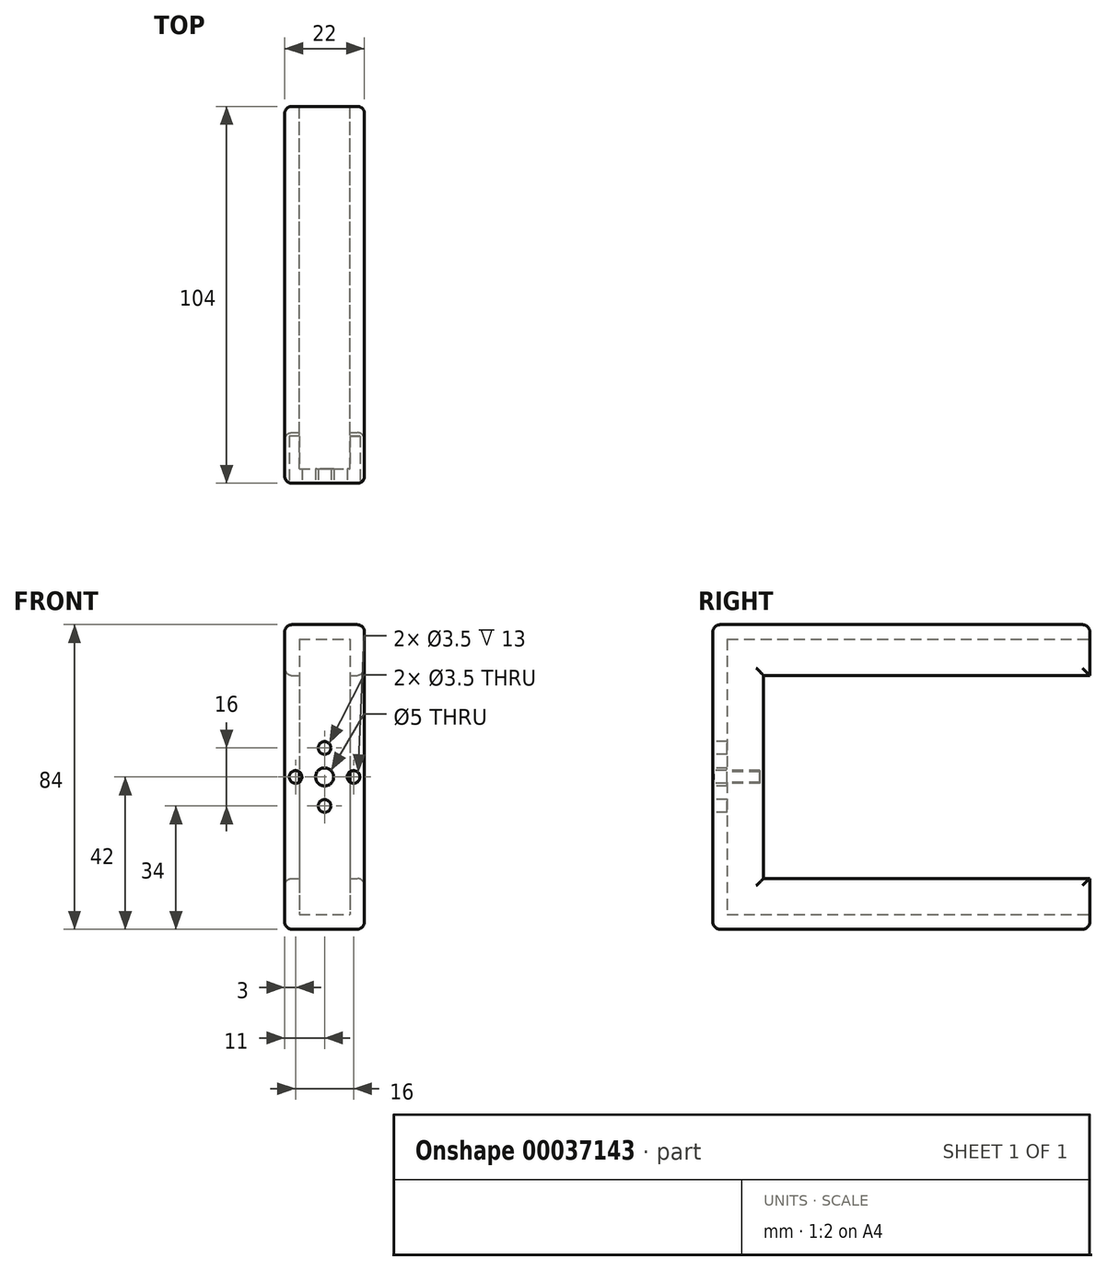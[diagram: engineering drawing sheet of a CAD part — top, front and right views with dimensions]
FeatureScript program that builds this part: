
annotation { "Feature Type Name" : "Feature", "Feature Type Description" : "" }
export const myFeature = defineFeature(function(context is Context, id is Id, definition is map)
    precondition{}
    {
        {
            var Q0;
            Q0=qCreatedBy(makeId("Front.planeOp"),FACE);
            var sketch = newSketch(context, id + "F0", { "sketchPlane" : qUnion([Q0])});
            skLineSegment(sketch, "E0.bottom", {"start": v(-7, 38) * mm, "end": v(7, 38) * mm});
            skLineSegment(sketch, "E0.top", {"start": v(-7, -38) * mm, "end": v(7, -38) * mm});
            skLineSegment(sketch, "E0.left", {"start": v(-7, 38) * mm, "end": v(-7, -38) * mm});
            skLineSegment(sketch, "E0.right", {"start": v(7, 38) * mm, "end": v(7, -38) * mm});
            skLineSegment(sketch, "E1.rect.bottom", {"start": v(-11, 42) * mm, "end": v(11, 42) * mm});
            skLineSegment(sketch, "E1.rect.top", {"start": v(-11, -42) * mm, "end": v(11, -42) * mm});
            skLineSegment(sketch, "E1.rect.left", {"start": v(-11, 42) * mm, "end": v(-11, -42) * mm});
            skLineSegment(sketch, "E1.rect.right", {"start": v(11, 42) * mm, "end": v(11, -42) * mm});
            skPoint(sketch, "E1.rect.middle", {"position": v(0, 0) * mm});
            skSolve(sketch);
        }
        {
            var Q0;
            Q0 = qSketchRegion(id + "F0", true);
            extrude(context, id + "F1", {"entities" : qUnion([Q0]), "depth" : 100 * mm});
        }
        {
            var Q0;
            Q0=makeQuery(id+"F1.opExtrude","CAP_FACE",FACE,{"disambiguationData":[OSD([sQuery(id+"F0.wireOp",EDGE,"E0.bottom"),sQuery(id+"F0.wireOp",EDGE,"E0.top"),sQuery(id+"F0.wireOp",EDGE,"E0.left"),sQuery(id+"F0.wireOp",EDGE,"E0.right"),sQuery(id+"F0.wireOp",EDGE,"E1.rect.bottom"),sQuery(id+"F0.wireOp",EDGE,"E1.rect.top"),sQuery(id+"F0.wireOp",EDGE,"E1.rect.left"),sQuery(id+"F0.wireOp",EDGE,"E1.rect.right")])],"isStart":false});
            var sketch = newSketch(context, id + "F2", { "sketchPlane" : qUnion([Q0])});
            skLineSegment(sketch, "E2.bottom", {"start": v(-11, 42) * mm, "end": v(11, 42) * mm});
            skLineSegment(sketch, "E2.top", {"start": v(-11, -42) * mm, "end": v(11, -42) * mm});
            skLineSegment(sketch, "E2.left", {"start": v(-11, 42) * mm, "end": v(-11, -42) * mm});
            skLineSegment(sketch, "E2.right", {"start": v(11, 42) * mm, "end": v(11, -42) * mm});
            skSolve(sketch);
        }
        {
            var Q0;
            Q0 = qSketchRegion(id + "F2", true);
            extrude(context, id + "F3", {"entities" : qUnion([Q0]), "operationType" : NewBodyOperationType.ADD, "depth" : 4 * mm});
        }
        {
            var Q0;
            Q0=makeQuery(id+"F3.opExtrude","CAP_FACE",FACE,{"disambiguationData":[OSD([sQuery(id+"F2.wireOp",EDGE,"E2.bottom"),sQuery(id+"F2.wireOp",EDGE,"E2.top"),sQuery(id+"F2.wireOp",EDGE,"E2.left"),sQuery(id+"F2.wireOp",EDGE,"E2.right")])],"isStart":false});
            var sketch = newSketch(context, id + "F4", { "sketchPlane" : qUnion([Q0])});
            skCircle(sketch, "E3", {"center": v(0, 0) * mm, "radius": 2.5 * mm});
            skCircle(sketch, "E4", {"center": v(0, 8) * mm, "radius": 1.75 * mm});
            skCircle(sketch, "E5.1.0", {"center": v(-8, 0) * mm, "radius": 1.75 * mm});
            skCircle(sketch, "E5.2.0", {"center": v(0, -8) * mm, "radius": 1.75 * mm});
            skCircle(sketch, "E5.3.0", {"center": v(8, 0) * mm, "radius": 1.75 * mm});
            skSolve(sketch);
        }
        {
            var Q0;
            Q0 = qSketchRegion(id + "F4", true);
            extrude(context, id + "F5", {"entities" : qUnion([Q0]), "operationType" : NewBodyOperationType.REMOVE, "oppositeDirection" : true, "depth" : 13 * mm});
        }
        {
            var Q0;
            Q0=makeQuery(id+"F3.boolean.opBoolean","MERGE",FACE,{"derivedFrom":[makeQuery(id+"F1.opExtrude","SWEPT_FACE",FACE,{"disambiguationData":[OSD([sQuery(id+"F0.wireOp",EDGE,"E1.rect.right")])]}),makeQuery(id+"F3.opExtrude","SWEPT_FACE",FACE,{"disambiguationData":[OSD([sQuery(id+"F2.wireOp",EDGE,"E2.right")])]})]});
            var sketch = newSketch(context, id + "F6", { "sketchPlane" : qUnion([Q0])});
            skLineSegment(sketch, "E6.bottom", {"start": v(-90, 28) * mm, "end": v(0, 28) * mm});
            skLineSegment(sketch, "E6.top", {"start": v(-90, -28) * mm, "end": v(0, -28) * mm});
            skLineSegment(sketch, "E6.left", {"start": v(-90, 28) * mm, "end": v(-90, -28) * mm});
            skLineSegment(sketch, "E6.right", {"start": v(0, 28) * mm, "end": v(0, -28) * mm});
            skSolve(sketch);
        }
        {
            var Q0;
            Q0 = qSketchRegion(id + "F6", true);
            extrude(context, id + "F7", {"entities" : qUnion([Q0]), "operationType" : NewBodyOperationType.REMOVE, "endBound" : BoundingType.THROUGH_ALL, "oppositeDirection" : true, "depth" : 25 * mm});
        }
        {
            var Q0;
            Q0=makeQuery(id+"F3.boolean.opBoolean","MERGE",FACE,{"derivedFrom":[makeQuery(id+"F1.opExtrude","SWEPT_FACE",FACE,{"disambiguationData":[OSD([sQuery(id+"F0.wireOp",EDGE,"E1.rect.right")])]}),makeQuery(id+"F3.opExtrude","SWEPT_FACE",FACE,{"disambiguationData":[OSD([sQuery(id+"F2.wireOp",EDGE,"E2.right")])]})]});
            var Q1;
            Q1=makeQuery(id+"F3.boolean.opBoolean","MERGE",FACE,{"derivedFrom":[makeQuery(id+"F1.opExtrude","SWEPT_FACE",FACE,{"disambiguationData":[OSD([sQuery(id+"F0.wireOp",EDGE,"E1.rect.left")])]}),makeQuery(id+"F3.opExtrude","SWEPT_FACE",FACE,{"disambiguationData":[OSD([sQuery(id+"F2.wireOp",EDGE,"E2.left")])]})]});
            var Q2;
            Q2=makeQuery(id+"F3.boolean.opBoolean","MERGE",FACE,{"derivedFrom":[makeQuery(id+"F1.opExtrude","SWEPT_FACE",FACE,{"disambiguationData":[OSD([sQuery(id+"F0.wireOp",EDGE,"E1.rect.bottom")])]}),makeQuery(id+"F3.opExtrude","SWEPT_FACE",FACE,{"disambiguationData":[OSD([sQuery(id+"F2.wireOp",EDGE,"E2.bottom")])]})]});
            var Q3;
            Q3=makeQuery(id+"F3.boolean.opBoolean","MERGE",FACE,{"derivedFrom":[makeQuery(id+"F1.opExtrude","SWEPT_FACE",FACE,{"disambiguationData":[OSD([sQuery(id+"F0.wireOp",EDGE,"E1.rect.top")])]}),makeQuery(id+"F3.opExtrude","SWEPT_FACE",FACE,{"disambiguationData":[OSD([sQuery(id+"F2.wireOp",EDGE,"E2.top")])]})]});
            fillet(context, id + "F8", {"entities" : qUnion([Q0, Q1, Q2, Q3]), "radius" : 2 * mm, "tangentPropagation" : true, "allowEdgeOverflow" : false});
        }
    });
